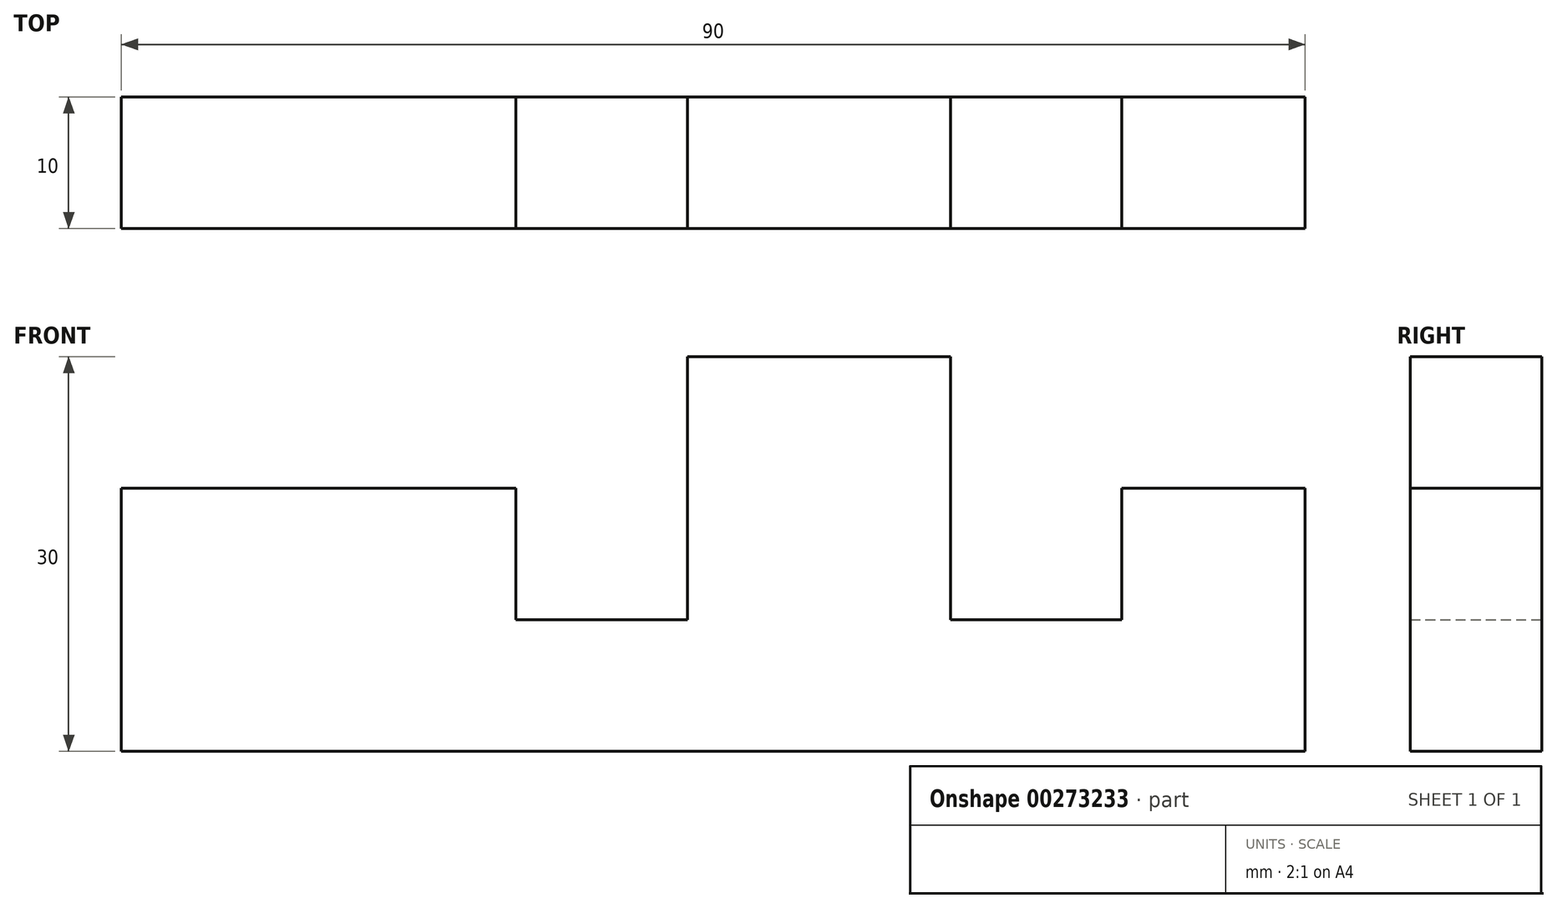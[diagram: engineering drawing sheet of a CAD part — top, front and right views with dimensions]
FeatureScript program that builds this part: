
annotation { "Feature Type Name" : "Feature", "Feature Type Description" : "" }
export const myFeature = defineFeature(function(context is Context, id is Id, definition is map)
    precondition{}
    {
        {
            var Q0;
            Q0=qCreatedBy(makeId("Front.planeOp"),FACE);
            var sketch = newSketch(context, id + "F0", { "sketchPlane" : qUnion([Q0])});
            skLineSegment(sketch, "E0", {"start": v(0, 0) * mm, "end": v(90, 0) * mm});
            skLineSegment(sketch, "E1", {"start": v(0, 0) * mm, "end": v(0, 20) * mm});
            skLineSegment(sketch, "E2", {"start": v(0, 20) * mm, "end": v(30, 20) * mm});
            skLineSegment(sketch, "E3", {"start": v(30, 20) * mm, "end": v(30, 10) * mm});
            skLineSegment(sketch, "E4", {"start": v(30, 10) * mm, "end": v(43.03, 10) * mm});
            skLineSegment(sketch, "E5", {"start": v(43.03, 10) * mm, "end": v(43.03, 30) * mm});
            skLineSegment(sketch, "E6", {"start": v(43.03, 30) * mm, "end": v(63.03, 30) * mm});
            skLineSegment(sketch, "E7", {"start": v(63.03, 30) * mm, "end": v(63.03, 10) * mm});
            skLineSegment(sketch, "E8", {"start": v(63.03, 10) * mm, "end": v(76.07, 10) * mm});
            skLineSegment(sketch, "E9", {"start": v(76.07, 10) * mm, "end": v(76.07, 20) * mm});
            skLineSegment(sketch, "E10", {"start": v(76.07, 20) * mm, "end": v(90, 20) * mm});
            skLineSegment(sketch, "E11", {"start": v(90, 20) * mm, "end": v(90, 0) * mm});
            skSolve(sketch);
        }
        {
            var Q0;
            Q0=makeQuery(id+"F0.imprint","IMPRINT",FACE,{"disambiguationData":[TD([[makeQuery(id+"F0.imprint","IMPRINT",EDGE,{"derivedFrom":sQuery(id+"F0.wireOp",EDGE,"E0")}),1.0]])]});
            extrude(context, id + "F1", {"entities" : qUnion([Q0]), "depth" : 10 * mm});
        }
    });
